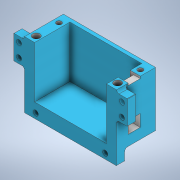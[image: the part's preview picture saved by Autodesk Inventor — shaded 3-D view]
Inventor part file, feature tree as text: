
AUTODESK INVENTOR PART (.ipt)
format: ipt  version: 2022 (Build 260153000, 153)  size: 513,024 bytes
history: native  units: mm
features: sketch x17, extrude x16, fillet x9, other x4, projected_geometry x4, mirror x1
ambient origin geometry x8: Origin, YZ Plane, XZ Plane, XY Plane, X Axis, Y Axis, Z Axis, Center Point
bodies: Body1 (feature_tree)
feature tree (51):
  other  "Твердое тело1"
  extrude  "Выдавливание1"  Depth=29.5mm
  extrude  "Выдавливание2"  Depth=60.0mm
  extrude  "Выдавливание3"  Depth=3.0mm
  other  "РабПлоскость1"
  other  "РабПлоскость2"
  extrude  "Выдавливание8"  Depth=43.0mm TaperAngle=0.0deg
  extrude  "Выдавливание9"  Depth=3.0mm TaperAngle=0.0deg
  extrude  "Выдавливание10"  Depth=4.2mm
  extrude  "Выдавливание13"  Depth=30.0mm TaperAngle=0.0deg
  other  "РабПлоскость6"
  mirror  "Зеркальное отражение5"
  extrude  "Выдавливание14"  [1 undecoded]
  extrude  "Выдавливание15"  Depth=8.3mm
  extrude  "Выдавливание16"  Depth=9.0mm
  fillet  "Сопряжение18"  Radius=9.0mm
  fillet  "Сопряжение19"  Radius=4.2mm
  fillet  "Сопряжение20"  Radius=7.0mm
  extrude  "Выдавливание17"  Depth=7.15mm
  extrude  "Выдавливание18"  Depth=3.0mm TaperAngle=0.0deg
  extrude  "Выдавливание20"  Depth=0.2mm
  extrude  "Выдавливание21"  Depth=0.2mm
  extrude  "Выдавливание22"  Depth=7.0mm TaperAngle=0.0deg
  extrude  "Выдавливание23"  Depth=0.2mm
  fillet  "Сопряжение16"  Radius=19.0mm
  fillet  "Сопряжение10"  Radius=68.0mm
  fillet  "Сопряжение6"  Radius=2.0mm
  fillet  "Сопряжение7"  Radius=10.0mm
  fillet  "Сопряжение14"  Radius=77.0mm
  fillet  "Сопряжение15"  Radius=5.0mm
  sketch  "Эскиз14"
  sketch  "Эскиз1"
  sketch  "Эскиз2"
  sketch  "Эскиз3"
  sketch  "Эскиз8"
  sketch  "Эскиз9"
  sketch  "Эскиз10"
  sketch  "Эскиз15"
  sketch  "Эскиз17"
  projected_geometry  "Спроецированная петля1"
  sketch  "Эскиз18"
  projected_geometry  "Спроецированная петля2"
  sketch  "Эскиз19"
  projected_geometry  "Спроецированная петля3"
  sketch  "Эскиз20"
  sketch  "Эскиз21"
  sketch  "Эскиз23"
  sketch  "Эскиз24"
  sketch  "Эскиз25"
  sketch  "Эскиз26"
  projected_geometry  "Спроецированная петля4"
note: 1 required parameter value undecoded (feature->parameter linkage not recoverable at this tier; creation-order binding heuristic only, values carry confidence <= 0.55)
